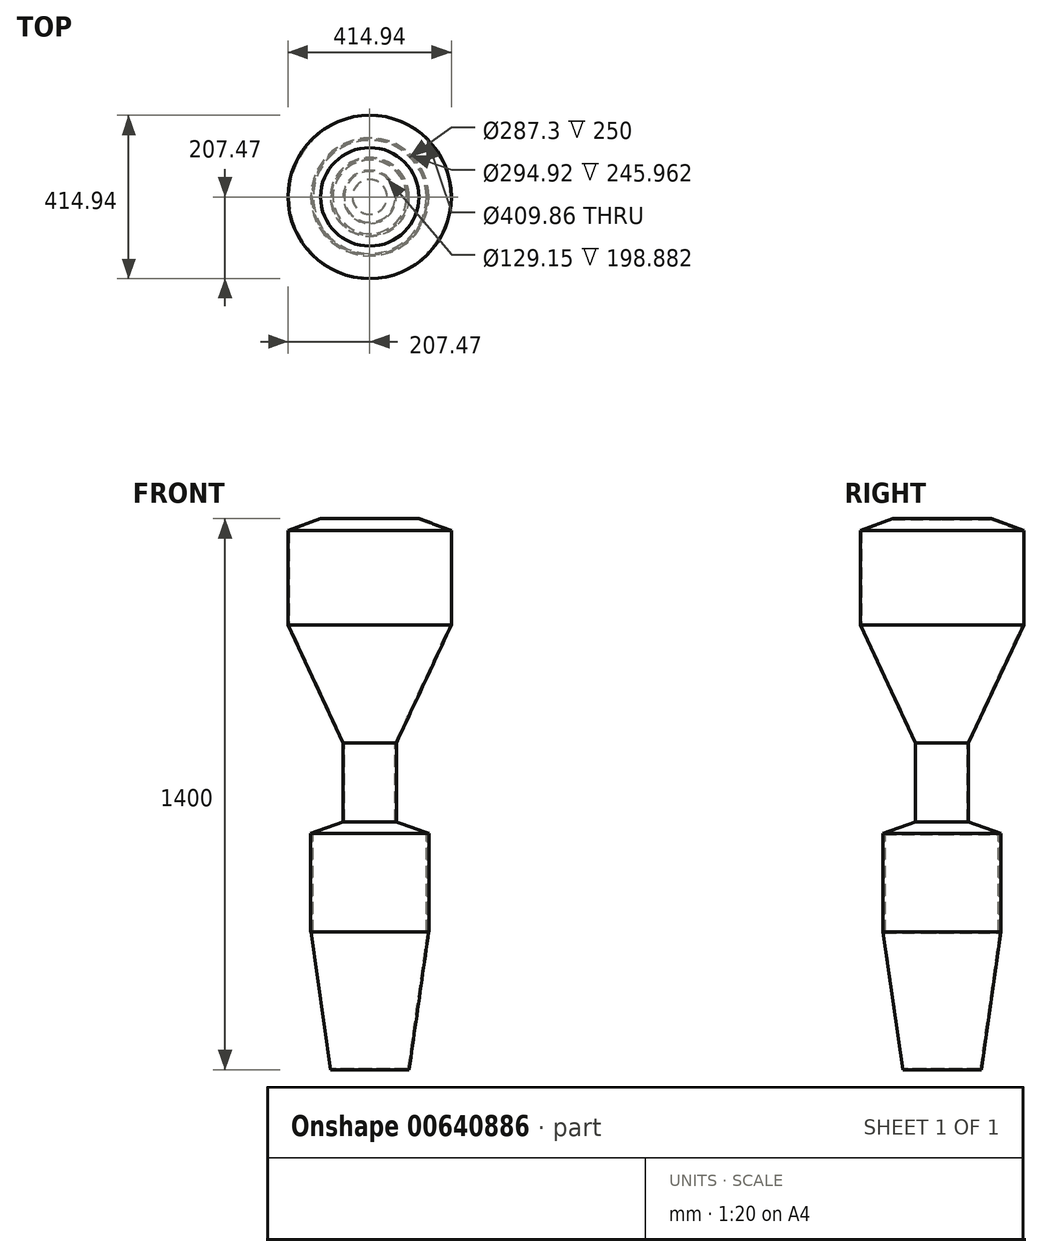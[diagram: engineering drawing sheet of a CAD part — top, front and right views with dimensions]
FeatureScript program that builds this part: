
annotation { "Feature Type Name" : "Feature", "Feature Type Description" : "" }
export const myFeature = defineFeature(function(context is Context, id is Id, definition is map)
    precondition{}
    {
        {
            var Q0;
            Q0=qCreatedBy(makeId("Top.planeOp"),FACE);
            var sketch = newSketch(context, id + "F0", { "sketchPlane" : qUnion([Q0])});
            skCircle(sketch, "E0", {"center": v(0, 0) * mm, "radius": 100 * mm});
            skCircle(sketch, "E1.0", {"center": v(0, 0) * mm, "radius": 93.65 * mm});
            skSolve(sketch);
        }
        {
            var Q0;
            Q0=qCreatedBy(makeId("Top.planeOp"),FACE);
            cPlane(context, id + "F1", {"entities" : qUnion([Q0]), "cplaneType" : CPlaneType.OFFSET, "offset" : 600 * mm, "width" : 152.4 * mm, "height" : 152.4 * mm});
        }
        {
            var Q0;
            Q0=qCreatedBy(id+"F1.planeOp",FACE);
            var sketch = newSketch(context, id + "F2", { "sketchPlane" : qUnion([Q0])});
            skCircle(sketch, "E2", {"center": v(0, 0) * mm, "radius": 150 * mm});
            skCircle(sketch, "E3.0", {"center": v(0, 0) * mm, "radius": 143.65 * mm});
            skSolve(sketch);
        }
        {
            var Q0;
            Q0=makeQuery(id+"F2.imprint","IMPRINT",FACE,{"disambiguationData":[TD([[makeQuery(id+"F2.imprint","IMPRINT",EDGE,{"derivedFrom":sQuery(id+"F2.wireOp",EDGE,"E2")}),1.0]])]});
            extrude(context, id + "F3", {"entities" : qUnion([Q0]), "oppositeDirection" : true, "depth" : 250 * mm, "offsetDistance" : 25.4 * mm});
        }
        {
            var Q0;
            Q0=makeQuery(id+"F0.imprint","IMPRINT",FACE,{"disambiguationData":[TD([[makeQuery(id+"F0.imprint","IMPRINT",EDGE,{"derivedFrom":sQuery(id+"F0.wireOp",EDGE,"E0")}),1.0]])]});
            var Q1;
            Q1=makeQuery(id+"F3.opExtrude","CAP_FACE",FACE,{"disambiguationData":[OSD([sQuery(id+"F2.wireOp",EDGE,"E2"),sQuery(id+"F2.wireOp",EDGE,"E3.0")])],"isStart":false});
            extrude(context, id + "F4", {"entities" : qUnion([Q0]), "operationType" : NewBodyOperationType.ADD, "endBound" : BoundingType.UP_TO_SURFACE, "depth" : 106.17 * mm, "endBoundEntityFace" : qUnion([Q1]), "offsetDistance" : 25.4 * mm, "hasDraft" : true, "draftAngle" : 8.1 * degree});
        }
        {
            var Q0;
            Q0=makeQuery(id+"F4.opExtrude","SWEPT_FACE",FACE,{"disambiguationData":[OSD([sQuery(id+"F0.wireOp",EDGE,"E1.0")])]});
            var Q1;
            {var subQ0=sQuery(id+"F2.wireOp",EDGE,"E3.0");Q1=makeQuery(id+"F4.boolean.opBoolean","SPLIT",FACE,{"disambiguationData":[TD([makeQuery(id+"F3.opExtrude","SWEPT_FACE",FACE,{"disambiguationData":[OSD([subQ0])]})])],"derivedFrom":makeQuery(id+"F4.opExtrude","CAP_FACE",FACE,{"disambiguationData":[OSD([sQuery(id+"F2.wireOp",EDGE,"E2"),subQ0])],"isStart":false})});}
            var Q2;
            Q2=makeQuery(id+"F3.opExtrude","SWEPT_BODY",BODY,{"disambiguationData":[OSD([sQuery(id+"F2.wireOp",EDGE,"E2"),sQuery(id+"F2.wireOp",EDGE,"E3.0")])]});
            shell(context, id + "F5", {"entities" : qUnion([Q0, Q1]), "parts" : qUnion([Q2]), "thickness" : 2.54 * mm});
        }
        {
            var Q0;
            Q0=qCreatedBy(id+"F1.planeOp",FACE);
            var sketch = newSketch(context, id + "F6", { "sketchPlane" : qUnion([Q0])});
            skCircle(sketch, "E4", {"center": v(0, 0) * mm, "radius": 150 * mm});
            skSolve(sketch);
        }
        {
            var Q0;
            Q0 = qSketchRegion(id + "F6", true);
            extrude(context, id + "F7", {"entities" : qUnion([Q0]), "depth" : 30 * mm, "offsetDistance" : 25.4 * mm, "hasDraft" : true, "draftAngle" : 70 * degree, "draftPullDirection" : true});
        }
        {
            var Q0;
            Q0=makeQuery(id+"F7.opExtrude","CAP_FACE",FACE,{"disambiguationData":[OSD([sQuery(id+"F6.wireOp",EDGE,"E4")])],"isStart":false});
            var sketch = newSketch(context, id + "F8", { "sketchPlane" : qUnion([Q0])});
            skCircle(sketch, "E5", {"center": v(0, 0) * mm, "radius": 67.58 * mm});
            skSolve(sketch);
        }
        {
            var Q0;
            Q0 = qSketchRegion(id + "F8", true);
            extrude(context, id + "F9", {"entities" : qUnion([Q0]), "operationType" : NewBodyOperationType.ADD, "depth" : 200 * mm, "offsetDistance" : 25.4 * mm});
        }
        {
            var Q0;
            Q0=makeQuery(id+"F9.opExtrude","CAP_FACE",FACE,{"disambiguationData":[OSD([sQuery(id+"F8.wireOp",EDGE,"E5")])],"isStart":false});
            var sketch = newSketch(context, id + "F10", { "sketchPlane" : qUnion([Q0])});
            skCircle(sketch, "E6", {"center": v(0, 0) * mm, "radius": 64.58 * mm});
            skSolve(sketch);
        }
        {
            var Q0;
            Q0=makeQuery(id+"F10.imprint","IMPRINT",FACE,{"disambiguationData":[TD([[makeQuery(id+"F10.imprint","IMPRINT",EDGE,{"derivedFrom":sQuery(id+"F10.wireOp",EDGE,"E6")}),1.0]])]});
            extrude(context, id + "F11", {"entities" : qUnion([Q0]), "operationType" : NewBodyOperationType.REMOVE, "oppositeDirection" : true, "depth" : 198.88 * mm, "offsetDistance" : 25.4 * mm});
        }
        {
            var Q0;
            Q0=makeQuery(id+"F9.opExtrude","CAP_FACE",FACE,{"disambiguationData":[OSD([sQuery(id+"F8.wireOp",EDGE,"E5")])],"isStart":false});
            var sketch = newSketch(context, id + "F12", { "sketchPlane" : qUnion([Q0])});
            skCircle(sketch, "E7", {"center": v(0, 0) * mm, "radius": 67.58 * mm});
            skSolve(sketch);
        }
        {
            var Q0;
            Q0 = qSketchRegion(id + "F12", true);
            extrude(context, id + "F13", {"entities" : qUnion([Q0]), "depth" : 300 * mm, "offsetDistance" : 25.4 * mm, "hasDraft" : true, "draftAngle" : 25 * degree});
        }
        {
            var Q0;
            Q0=makeQuery(id+"F13.opExtrude","CAP_FACE",FACE,{"disambiguationData":[OSD([sQuery(id+"F12.wireOp",EDGE,"E7")])],"isStart":false});
            var sketch = newSketch(context, id + "F14", { "sketchPlane" : qUnion([Q0])});
            skCircle(sketch, "E8", {"center": v(0, 0) * mm, "radius": 207.47 * mm});
            skSolve(sketch);
        }
        {
            var Q0;
            Q0 = qSketchRegion(id + "F14", true);
            extrude(context, id + "F15", {"entities" : qUnion([Q0]), "operationType" : NewBodyOperationType.ADD, "depth" : 240 * mm, "offsetDistance" : 25.4 * mm});
        }
        {
            var Q0;
            Q0=makeQuery(id+"F15.opExtrude","CAP_FACE",FACE,{"disambiguationData":[OSD([sQuery(id+"F14.wireOp",EDGE,"E8")])],"isStart":false});
            var sketch = newSketch(context, id + "F16", { "sketchPlane" : qUnion([Q0])});
            skCircle(sketch, "E9", {"center": v(0, 0) * mm, "radius": 207.47 * mm});
            skSolve(sketch);
        }
        {
            var Q0;
            Q0 = qSketchRegion(id + "F16", true);
            extrude(context, id + "F17", {"entities" : qUnion([Q0]), "operationType" : NewBodyOperationType.ADD, "depth" : 30 * mm, "offsetDistance" : 25.4 * mm, "hasDraft" : true, "draftAngle" : 70 * degree, "draftPullDirection" : true});
        }
        {
            var Q0;
            Q0=makeQuery(id+"F13.opExtrude","CAP_FACE",FACE,{"disambiguationData":[OSD([sQuery(id+"F12.wireOp",EDGE,"E7")])],"isStart":true});
            shell(context, id + "F18", {"entities" : qUnion([Q0]), "thickness" : 2.54 * mm});
        }
    });
